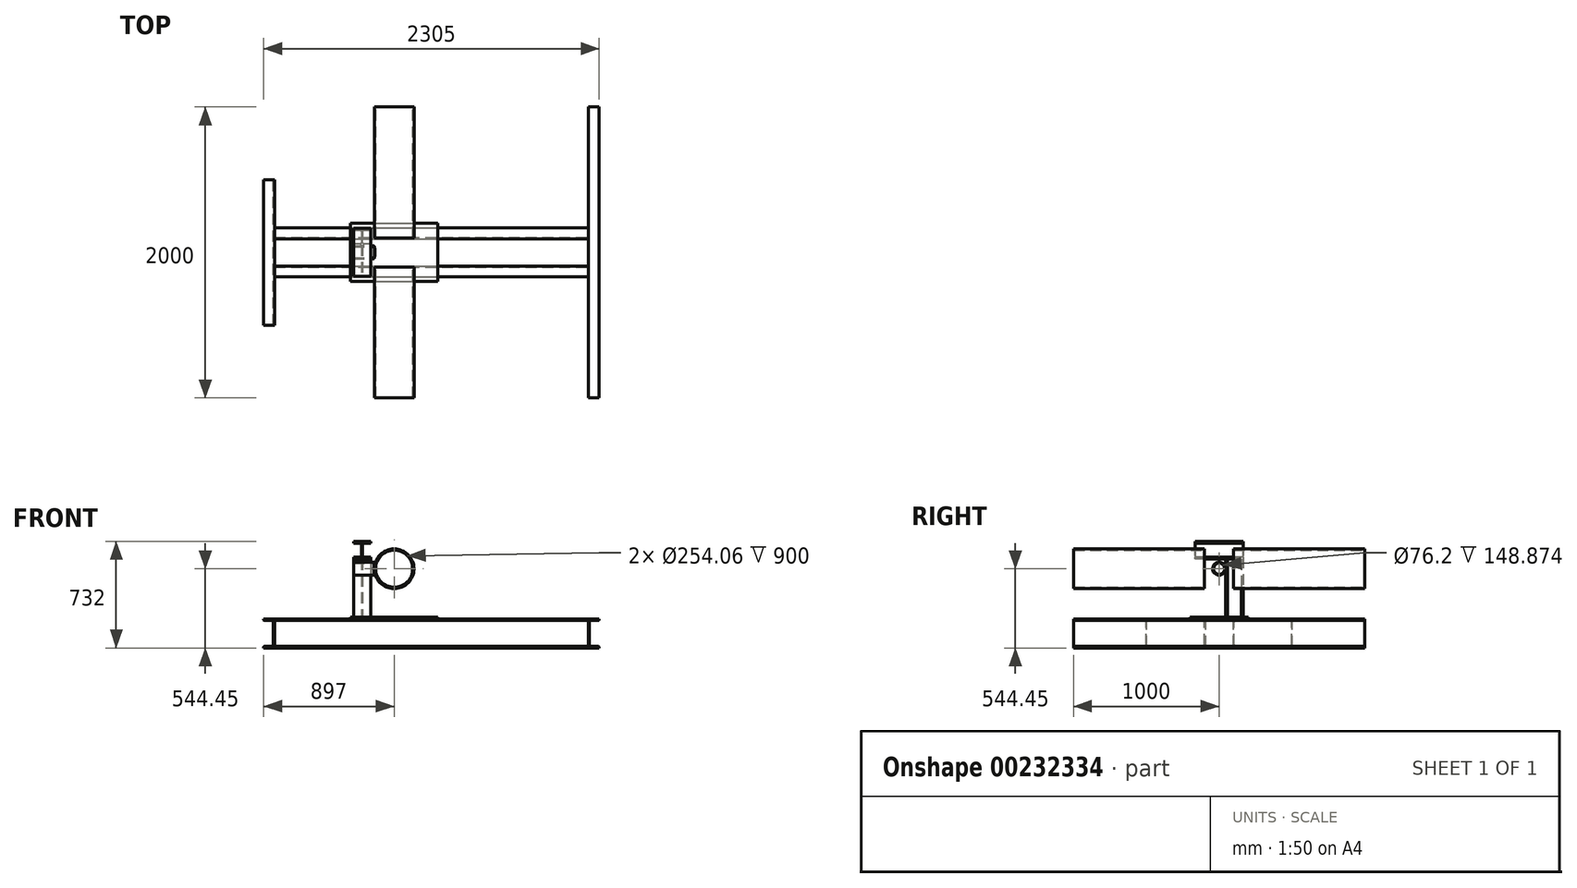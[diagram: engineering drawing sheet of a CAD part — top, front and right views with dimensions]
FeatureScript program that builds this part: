
annotation { "Feature Type Name" : "Feature", "Feature Type Description" : "" }
export const myFeature = defineFeature(function(context is Context, id is Id, definition is map)
    precondition{}
    {
        {
            var Q0;
            Q0=qCreatedBy(makeId("Front.planeOp"),FACE);
            var sketch = newSketch(context, id + "F0", { "sketchPlane" : qUnion([Q0])});
            skCircle(sketch, "E0", {"center": v(0, 0) * mm, "radius": 136.55 * mm});
            skCircle(sketch, "E1", {"center": v(0, 0) * mm, "radius": 127.03 * mm});
            skSolve(sketch);
        }
        {
            var Q0;
            Q0=makeQuery(id+"F0.imprint","IMPRINT",FACE,{"disambiguationData":[TD([[makeQuery(id+"F0.imprint","IMPRINT",EDGE,{"derivedFrom":sQuery(id+"F0.wireOp",EDGE,"E0")}),1.0]])]});
            extrude(context, id + "F1", {"entities" : qUnion([Q0]), "endBound" : BoundingType.SYMMETRIC, "depth" : 2000 * mm});
        }
        {
            var Q0;
            Q0=qCreatedBy(makeId("Right.planeOp"),FACE);
            var sketch = newSketch(context, id + "F2", { "sketchPlane" : qUnion([Q0])});
            skCircle(sketch, "E2", {"center": v(0, 0) * mm, "radius": 44.45 * mm});
            skCircle(sketch, "E3", {"center": v(0, 0) * mm, "radius": 38.1 * mm});
            skSolve(sketch);
        }
        {
            var Q0;
            Q0=qCreatedBy(makeId("Right.planeOp"),FACE);
            var sketch = newSketch(context, id + "F3", { "sketchPlane" : qUnion([Q0])});
            skLineSegment(sketch, "E4", {"start": v(-169, -344.45) * mm, "end": v(-94, -344.45) * mm});
            skLineSegment(sketch, "E5", {"start": v(-94, -344.45) * mm, "end": v(-94, -544.45) * mm});
            skLineSegment(sketch, "E6", {"start": v(-94, -544.45) * mm, "end": v(-169, -544.45) * mm});
            skLineSegment(sketch, "E7", {"start": v(-169, -544.45) * mm, "end": v(-169, -538.95) * mm});
            skLineSegment(sketch, "E8", {"start": v(-163, -532.95) * mm, "end": v(-114, -532.95) * mm});
            skLineSegment(sketch, "E9", {"start": v(-102.5, -521.45) * mm, "end": v(-102.5, -367.45) * mm});
            skLineSegment(sketch, "E10", {"start": v(-114, -355.95) * mm, "end": v(-163, -355.95) * mm});
            skLineSegment(sketch, "E11", {"start": v(-169, -349.95) * mm, "end": v(-169, -344.45) * mm});
            skPoint(sketch, "E12.visualSharp", {"position": v(-102.5, -355.95) * mm});
            skArc(sketch, "E12.filletArc", {"start": v(-102.5, -367.45) * mm, "mid": v(-105.87, -359.32) * mm, "end": v(-114, -355.95) * mm});
            skPoint(sketch, "E13.visualSharp", {"position": v(-102.5, -532.95) * mm});
            skArc(sketch, "E13.filletArc", {"start": v(-114, -532.95) * mm, "mid": v(-105.87, -529.58) * mm, "end": v(-102.5, -521.45) * mm});
            skPoint(sketch, "E14.visualSharp", {"position": v(-169, -355.95) * mm});
            skArc(sketch, "E14.filletArc", {"start": v(-169, -349.95) * mm, "mid": v(-167.24, -354.2) * mm, "end": v(-163, -355.95) * mm});
            skPoint(sketch, "E15.visualSharp", {"position": v(-169, -532.95) * mm});
            skArc(sketch, "E15.filletArc", {"start": v(-163, -532.95) * mm, "mid": v(-167.24, -534.7) * mm, "end": v(-169, -538.95) * mm});
            skLineSegment(sketch, "E16", {"start": v(0, 0) * mm, "end": v(0, -750.46) * mm, "construction": true});
            skSolve(sketch);
        }
        {
            var Q0;
            Q0=makeQuery(id+"F3.imprint","IMPRINT",FACE,{"disambiguationData":[TD([[makeQuery(id+"F3.imprint","IMPRINT",EDGE,{"derivedFrom":sQuery(id+"F3.wireOp",EDGE,"E4")}),-1.0]])]});
            extrude(context, id + "F4", {"entities" : qUnion([Q0]), "oppositeDirection" : true, "depth" : 822 * mm, "hasSecondDirection" : true, "secondDirectionOppositeDirection" : false, "secondDirectionDepth" : (2155 - 822) * mm});
        }
        {
            var Q0;
            Q0=makeQuery(id+"F4.opExtrude","SWEPT_BODY",BODY,{"disambiguationData":[OSD([sQuery(id+"F3.wireOp",EDGE,"E4"),sQuery(id+"F3.wireOp",EDGE,"E5"),sQuery(id+"F3.wireOp",EDGE,"E6"),sQuery(id+"F3.wireOp",EDGE,"E7"),sQuery(id+"F3.wireOp",EDGE,"E8"),sQuery(id+"F3.wireOp",EDGE,"E9"),sQuery(id+"F3.wireOp",EDGE,"E10"),sQuery(id+"F3.wireOp",EDGE,"E11"),sQuery(id+"F3.wireOp",EDGE,"E12.filletArc"),sQuery(id+"F3.wireOp",EDGE,"E13.filletArc"),sQuery(id+"F3.wireOp",EDGE,"E14.filletArc"),sQuery(id+"F3.wireOp",EDGE,"E15.filletArc")])]});
            var Q1;
            Q1=qCreatedBy(makeId("Front.planeOp"),FACE);
            mirror(context, id + "F5", {"entities" : qUnion([Q0]), "mirrorPlane" : qUnion([Q1])});
        }
        {
            var Q0;
            Q0=qCreatedBy(makeId("Front.planeOp"),FACE);
            var sketch = newSketch(context, id + "F6", { "sketchPlane" : qUnion([Q0])});
            skLineSegment(sketch, "E17", {"start": v(-897, -344.45) * mm, "end": v(-822, -344.45) * mm});
            skLineSegment(sketch, "E18", {"start": v(-822, -344.45) * mm, "end": v(-822, -544.45) * mm});
            skLineSegment(sketch, "E19", {"start": v(-822, -544.45) * mm, "end": v(-897, -544.45) * mm});
            skLineSegment(sketch, "E20", {"start": v(-897, -544.45) * mm, "end": v(-897, -538.95) * mm});
            skLineSegment(sketch, "E21", {"start": v(-891, -532.95) * mm, "end": v(-842, -532.95) * mm});
            skLineSegment(sketch, "E22", {"start": v(-830.5, -521.45) * mm, "end": v(-830.5, -367.45) * mm});
            skLineSegment(sketch, "E23", {"start": v(-842, -355.95) * mm, "end": v(-891, -355.95) * mm});
            skLineSegment(sketch, "E24", {"start": v(-897, -349.95) * mm, "end": v(-897, -344.45) * mm});
            skPoint(sketch, "E25.visualSharp", {"position": v(-830.5, -355.95) * mm});
            skArc(sketch, "E25.filletArc", {"start": v(-830.5, -367.45) * mm, "mid": v(-833.87, -359.32) * mm, "end": v(-842, -355.95) * mm});
            skPoint(sketch, "E26.visualSharp", {"position": v(-830.5, -532.95) * mm});
            skArc(sketch, "E26.filletArc", {"start": v(-842, -532.95) * mm, "mid": v(-833.87, -529.58) * mm, "end": v(-830.5, -521.45) * mm});
            skPoint(sketch, "E27.visualSharp", {"position": v(-897, -355.95) * mm});
            skArc(sketch, "E27.filletArc", {"start": v(-897, -349.95) * mm, "mid": v(-895.24, -354.2) * mm, "end": v(-891, -355.95) * mm});
            skPoint(sketch, "E28.visualSharp", {"position": v(-897, -532.95) * mm});
            skArc(sketch, "E28.filletArc", {"start": v(-891, -532.95) * mm, "mid": v(-895.24, -534.7) * mm, "end": v(-897, -538.95) * mm});
            skLineSegment(sketch, "E29", {"start": v(1258, -344.45) * mm, "end": v(1333, -344.45) * mm});
            skLineSegment(sketch, "E30", {"start": v(1333, -344.45) * mm, "end": v(1333, -544.45) * mm});
            skLineSegment(sketch, "E31", {"start": v(1333, -544.45) * mm, "end": v(1258, -544.45) * mm});
            skLineSegment(sketch, "E32", {"start": v(1258, -544.45) * mm, "end": v(1258, -538.95) * mm});
            skLineSegment(sketch, "E33", {"start": v(1264, -532.95) * mm, "end": v(1313, -532.95) * mm});
            skLineSegment(sketch, "E34", {"start": v(1324.5, -521.45) * mm, "end": v(1324.5, -367.45) * mm});
            skLineSegment(sketch, "E35", {"start": v(1313, -355.95) * mm, "end": v(1264, -355.95) * mm});
            skLineSegment(sketch, "E36", {"start": v(1258, -349.95) * mm, "end": v(1258, -344.45) * mm});
            skPoint(sketch, "E37.visualSharp", {"position": v(1324.5, -355.95) * mm});
            skArc(sketch, "E37.filletArc", {"start": v(1324.5, -367.45) * mm, "mid": v(1321.13, -359.32) * mm, "end": v(1313, -355.95) * mm});
            skPoint(sketch, "E38.visualSharp", {"position": v(1324.5, -532.95) * mm});
            skArc(sketch, "E38.filletArc", {"start": v(1313, -532.95) * mm, "mid": v(1321.13, -529.58) * mm, "end": v(1324.5, -521.45) * mm});
            skPoint(sketch, "E39.visualSharp", {"position": v(1258, -355.95) * mm});
            skArc(sketch, "E39.filletArc", {"start": v(1258, -349.95) * mm, "mid": v(1259.76, -354.2) * mm, "end": v(1264, -355.95) * mm});
            skPoint(sketch, "E40.visualSharp", {"position": v(1258, -532.95) * mm});
            skArc(sketch, "E40.filletArc", {"start": v(1264, -532.95) * mm, "mid": v(1259.76, -534.7) * mm, "end": v(1258, -538.95) * mm});
            skLineSegment(sketch, "E41.MirrorCS", {"start": v(1408, -544.45) * mm, "end": v(1408, -538.95) * mm});
            skLineSegment(sketch, "E42.MirrorCS", {"start": v(1408, -349.95) * mm, "end": v(1408, -344.45) * mm});
            skArc(sketch, "E43.MirrorCS", {"start": v(1402, -532.95) * mm, "mid": v(1406.24, -534.7) * mm, "end": v(1408, -538.95) * mm});
            skArc(sketch, "E44.MirrorCS", {"start": v(1408, -349.95) * mm, "mid": v(1406.24, -354.2) * mm, "end": v(1402, -355.95) * mm});
            skArc(sketch, "E45.MirrorCS", {"start": v(1353, -532.95) * mm, "mid": v(1344.87, -529.58) * mm, "end": v(1341.5, -521.45) * mm});
            skArc(sketch, "E46.MirrorCS", {"start": v(1341.5, -367.45) * mm, "mid": v(1344.87, -359.32) * mm, "end": v(1353, -355.95) * mm});
            skLineSegment(sketch, "E47.MirrorCS", {"start": v(1333, -544.45) * mm, "end": v(1408, -544.45) * mm});
            skLineSegment(sketch, "E48.MirrorCS", {"start": v(1341.5, -521.45) * mm, "end": v(1341.5, -367.45) * mm});
            skPoint(sketch, "E49.MirrorP", {"position": v(1408, -355.95) * mm});
            skPoint(sketch, "E50.MirrorP", {"position": v(1341.5, -532.95) * mm});
            skPoint(sketch, "E51.MirrorP", {"position": v(1408, -532.95) * mm});
            skLineSegment(sketch, "E52.MirrorCS", {"start": v(1353, -355.95) * mm, "end": v(1402, -355.95) * mm});
            skLineSegment(sketch, "E53.MirrorCS", {"start": v(1408, -344.45) * mm, "end": v(1333, -344.45) * mm});
            skLineSegment(sketch, "E54.MirrorCS", {"start": v(1402, -532.95) * mm, "end": v(1353, -532.95) * mm});
            skSolve(sketch);
        }
        {
            var Q0;
            Q0=makeQuery(id+"F6.imprint","IMPRINT",FACE,{"disambiguationData":[TD([[makeQuery(id+"F6.imprint","IMPRINT",EDGE,{"derivedFrom":sQuery(id+"F6.wireOp",EDGE,"E17")}),-1.0]])]});
            extrude(context, id + "F7", {"entities" : qUnion([Q0]), "endBound" : BoundingType.SYMMETRIC, "depth" : 1000 * mm});
        }
        {
            var Q0;
            Q0=makeQuery(id+"F6.imprint","IMPRINT",FACE,{"disambiguationData":[TD([[makeQuery(id+"F6.imprint","IMPRINT",EDGE,{"derivedFrom":sQuery(id+"F6.wireOp",EDGE,"E30")}),1.0]])]});
            extrude(context, id + "F8", {"entities" : qUnion([Q0]), "endBound" : BoundingType.SYMMETRIC, "depth" : 2000 * mm});
        }
        {
            var Q0;
            Q0=makeQuery(id+"F5.opPattern","COPY",FACE,{"derivedFrom":makeQuery(id+"F4.opExtrude","SWEPT_FACE",FACE,{"disambiguationData":[OSD([sQuery(id+"F3.wireOp",EDGE,"E4")])]}),"instanceName":"1"});
            var sketch = newSketch(context, id + "F9", { "sketchPlane" : qUnion([Q0])});
            skLineSegment(sketch, "E55.bottom", {"start": v(-300, 200) * mm, "end": v(300, 200) * mm});
            skLineSegment(sketch, "E55.top", {"start": v(-300, -200) * mm, "end": v(300, -200) * mm});
            skLineSegment(sketch, "E55.left", {"start": v(-300, 200) * mm, "end": v(-300, -200) * mm});
            skLineSegment(sketch, "E55.right", {"start": v(300, 200) * mm, "end": v(300, -200) * mm});
            skLineSegment(sketch, "E56", {"start": v(-300, 200) * mm, "end": v(300, -200) * mm, "construction": true});
            skSolve(sketch);
        }
        {
            var Q0;
            {var subQ0=sQuery(id+"F9.wireOp",EDGE,"E55.top");Q0=makeQuery(id+"F9.imprint","IMPRINT",FACE,{"disambiguationData":[TD([[makeQuery(id+"F9.imprint","IMPRINT",EDGE,{"derivedFrom":subQ0}),1.0]])]});}
            var Q1;
            {var subQ0=sQuery(id+"F9.wireOp",EDGE,"E55.bottom");Q1=makeQuery(id+"F9.imprint","IMPRINT",FACE,{"disambiguationData":[TD([[makeQuery(id+"F9.imprint","IMPRINT",EDGE,{"derivedFrom":subQ0}),-1.0]])]});}
            var Q2;
            {var subQ0=sQuery(id+"F9.wireOp",EDGE,"E55.left");var subQ1=sQuery(id+"F3.wireOp",EDGE,"E4");var subQ2=makeQuery(id+"F5.opPattern","COPY",EDGE,{"derivedFrom":makeQuery(id+"F4.opExtrude","SWEPT_EDGE",EDGE,{"disambiguationData":[OSD([subQ1,sQuery(id+"F3.wireOp",EDGE,"E11")])]}),"instanceName":"1"});var subQ3=makeQuery(id+"F9.imprint","INTERSECT",VERTEX,{"derivedFrom":[subQ2,subQ0]});Q2=makeQuery(id+"F9.imprint","IMPRINT",FACE,{"disambiguationData":[TD([[makeQuery(id+"F9.imprint","IMPRINT",EDGE,{"disambiguationData":[TD([[subQ3,-1.0]])],"derivedFrom":subQ0}),1.0]])]});}
            extrude(context, id + "F10", {"entities" : qUnion([Q0, Q1, Q2]), "depth" : 12 * mm});
        }
        {
            var Q0;
            Q0=makeQuery(id+"F10.opExtrude","CAP_FACE",FACE,{"disambiguationData":[OSD([sQuery(id+"F9.wireOp",EDGE,"E55.bottom"),sQuery(id+"F9.wireOp",EDGE,"E55.top"),sQuery(id+"F9.wireOp",EDGE,"E55.left"),sQuery(id+"F9.wireOp",EDGE,"E55.right")])],"isStart":false});
            var sketch = newSketch(context, id + "F11", { "sketchPlane" : qUnion([Q0])});
            skLineSegment(sketch, "E57", {"start": v(-280, 45) * mm, "end": v(-160, 45) * mm});
            skLineSegment(sketch, "E58", {"start": v(-160, 45) * mm, "end": v(-160, 56) * mm});
            skLineSegment(sketch, "E59", {"start": v(-160, 56) * mm, "end": v(-204.75, 56) * mm});
            skLineSegment(sketch, "E60", {"start": v(-216.75, 68) * mm, "end": v(-216.75, 142) * mm});
            skLineSegment(sketch, "E61", {"start": v(-204.75, 154) * mm, "end": v(-160, 154) * mm});
            skLineSegment(sketch, "E62", {"start": v(-160, 154) * mm, "end": v(-160, 165) * mm});
            skLineSegment(sketch, "E63", {"start": v(-160, 165) * mm, "end": v(-280, 165) * mm});
            skLineSegment(sketch, "E64", {"start": v(-280, 165) * mm, "end": v(-280, 154) * mm});
            skLineSegment(sketch, "E65", {"start": v(-280, 154) * mm, "end": v(-235.25, 154) * mm});
            skLineSegment(sketch, "E66", {"start": v(-223.25, 142) * mm, "end": v(-223.25, 68) * mm});
            skLineSegment(sketch, "E67", {"start": v(-235.25, 56) * mm, "end": v(-280, 56) * mm});
            skLineSegment(sketch, "E68", {"start": v(-280, 56) * mm, "end": v(-280, 45) * mm});
            skLineSegment(sketch, "E69", {"start": v(-220, 165) * mm, "end": v(-220, 45) * mm, "construction": true});
            skPoint(sketch, "E70.visualSharp", {"position": v(-223.25, 154) * mm});
            skArc(sketch, "E70.filletArc", {"start": v(-223.25, 142) * mm, "mid": v(-226.76, 150.49) * mm, "end": v(-235.25, 154) * mm});
            skPoint(sketch, "E71.visualSharp", {"position": v(-216.75, 154) * mm});
            skArc(sketch, "E71.filletArc", {"start": v(-204.75, 154) * mm, "mid": v(-213.24, 150.49) * mm, "end": v(-216.75, 142) * mm});
            skPoint(sketch, "E72.visualSharp", {"position": v(-223.25, 56) * mm});
            skArc(sketch, "E72.filletArc", {"start": v(-235.25, 56) * mm, "mid": v(-226.76, 59.51) * mm, "end": v(-223.25, 68) * mm});
            skPoint(sketch, "E73.visualSharp", {"position": v(-216.75, 56) * mm});
            skArc(sketch, "E73.filletArc", {"start": v(-216.75, 68) * mm, "mid": v(-213.24, 59.51) * mm, "end": v(-204.75, 56) * mm});
            skLineSegment(sketch, "E74", {"start": v(0, 0) * mm, "end": v(-497.1, 0) * mm, "construction": true});
            skPoint(sketch, "E74.endSnap0", {"position": v(-300, 0) * mm});
            skLineSegment(sketch, "E75", {"start": v(0, 0) * mm, "end": v(0, 277.06) * mm, "construction": true});
            skSolve(sketch);
        }
        {
            var Q0;
            Q0=makeQuery(id+"F11.imprint","IMPRINT",FACE,{"disambiguationData":[TD([[makeQuery(id+"F11.imprint","IMPRINT",EDGE,{"derivedFrom":sQuery(id+"F11.wireOp",EDGE,"E57")}),1.0]])]});
            extrude(context, id + "F12", {"entities" : qUnion([Q0]), "depth" : 400 * mm});
        }
        {
            var Q0;
            Q0=makeQuery(id+"F2.imprint","IMPRINT",FACE,{"disambiguationData":[TD([[makeQuery(id+"F2.imprint","IMPRINT",EDGE,{"derivedFrom":sQuery(id+"F2.wireOp",EDGE,"E2")}),1.0]])]});
            var Q1;
            Q1=makeQuery(id+"F12.opExtrude","SWEPT_FACE",FACE,{"disambiguationData":[OSD([sQuery(id+"F11.wireOp",EDGE,"E68")])]});
            extrude(context, id + "F13", {"entities" : qUnion([Q0]), "endBound" : BoundingType.UP_TO_SURFACE, "oppositeDirection" : true, "endBoundEntityFace" : qUnion([Q1]), "depth" : 320 * mm});
        }
        {
            var Q0;
            Q0=makeQuery(id+"F0.imprint","IMPRINT",FACE,{"disambiguationData":[TD([[makeQuery(id+"F0.imprint","IMPRINT",EDGE,{"derivedFrom":sQuery(id+"F0.wireOp",EDGE,"E1")}),1.0]])]});
            var Q1;
            Q1=makeQuery(id+"F0.imprint","IMPRINT",FACE,{"disambiguationData":[TD([[makeQuery(id+"F0.imprint","IMPRINT",EDGE,{"derivedFrom":sQuery(id+"F0.wireOp",EDGE,"E0")}),1.0]])]});
            extrude(context, id + "F14", {"entities" : qUnion([Q0, Q1]), "operationType" : NewBodyOperationType.REMOVE, "endBound" : BoundingType.SYMMETRIC, "oppositeDirection" : true, "depth" : 200 * mm});
        }
        {
            var Q0;
            Q0=makeQuery(id+"F14.boolean.opBoolean","INTERSECT",EDGE,{"derivedFrom":[makeQuery(id+"F13.opExtrude","SWEPT_FACE",FACE,{"disambiguationData":[OSD([sQuery(id+"F2.wireOp",EDGE,"E2")])]}),makeQuery(id+"F14.opExtrude","SWEPT_FACE",FACE,{"disambiguationData":[OSD([sQuery(id+"F0.wireOp",EDGE,"E0")])]})]});
            chamfer(context, id + "F15", {"entities" : qUnion([Q0]), "width" : 4 * mm, "tangentPropagation" : true});
        }
        {
            var Q0;
            Q0=qCreatedBy(makeId("Front.planeOp"),FACE);
            var sketch = newSketch(context, id + "F16", { "sketchPlane" : qUnion([Q0])});
            skLineSegment(sketch, "E76", {"start": v(-280, 67.55) * mm, "end": v(-160, 67.55) * mm});
            skLineSegment(sketch, "E77", {"start": v(-160, 67.55) * mm, "end": v(-160, 78.55) * mm});
            skLineSegment(sketch, "E78", {"start": v(-160, 78.55) * mm, "end": v(-204.75, 78.55) * mm});
            skLineSegment(sketch, "E79", {"start": v(-216.75, 90.55) * mm, "end": v(-216.75, 164.55) * mm});
            skLineSegment(sketch, "E80", {"start": v(-204.75, 176.55) * mm, "end": v(-160, 176.55) * mm});
            skLineSegment(sketch, "E81", {"start": v(-160, 176.55) * mm, "end": v(-160, 187.55) * mm});
            skLineSegment(sketch, "E82", {"start": v(-160, 187.55) * mm, "end": v(-280, 187.55) * mm});
            skLineSegment(sketch, "E83", {"start": v(-280, 187.55) * mm, "end": v(-280, 176.55) * mm});
            skLineSegment(sketch, "E84", {"start": v(-280, 176.55) * mm, "end": v(-235.25, 176.55) * mm});
            skLineSegment(sketch, "E85", {"start": v(-223.25, 164.55) * mm, "end": v(-223.25, 90.55) * mm});
            skLineSegment(sketch, "E86", {"start": v(-235.25, 78.55) * mm, "end": v(-280, 78.55) * mm});
            skLineSegment(sketch, "E87", {"start": v(-280, 78.55) * mm, "end": v(-280, 67.55) * mm});
            skLineSegment(sketch, "E88", {"start": v(-220, 187.55) * mm, "end": v(-220, 67.55) * mm, "construction": true});
            skPoint(sketch, "E89.visualSharp", {"position": v(-223.25, 176.55) * mm});
            skArc(sketch, "E89.filletArc", {"start": v(-223.25, 164.55) * mm, "mid": v(-226.76, 173.04) * mm, "end": v(-235.25, 176.55) * mm});
            skPoint(sketch, "E90.visualSharp", {"position": v(-216.75, 176.55) * mm});
            skArc(sketch, "E90.filletArc", {"start": v(-204.75, 176.55) * mm, "mid": v(-213.24, 173.04) * mm, "end": v(-216.75, 164.55) * mm});
            skPoint(sketch, "E91.visualSharp", {"position": v(-223.25, 78.55) * mm});
            skArc(sketch, "E91.filletArc", {"start": v(-235.25, 78.55) * mm, "mid": v(-226.76, 82.06) * mm, "end": v(-223.25, 90.55) * mm});
            skPoint(sketch, "E92.visualSharp", {"position": v(-216.75, 78.55) * mm});
            skArc(sketch, "E92.filletArc", {"start": v(-216.75, 90.55) * mm, "mid": v(-213.24, 82.06) * mm, "end": v(-204.75, 78.55) * mm});
            skSolve(sketch);
        }
        {
            var Q0;
            Q0=makeQuery(id+"F16.imprint","IMPRINT",FACE,{"disambiguationData":[TD([[makeQuery(id+"F16.imprint","IMPRINT",EDGE,{"derivedFrom":sQuery(id+"F16.wireOp",EDGE,"E76")}),1.0]])]});
            var Q1;
            Q1=makeQuery(id+"F12.opExtrude","SWEPT_FACE",FACE,{"disambiguationData":[OSD([sQuery(id+"F11.wireOp",EDGE,"E63")])]});
            extrude(context, id + "F17", {"entities" : qUnion([Q0]), "endBound" : BoundingType.UP_TO_SURFACE, "oppositeDirection" : true, "endBoundEntityFace" : qUnion([Q1]), "depth" : 25 * mm});
        }
        {
            var Q0;
            Q0=makeQuery(id+"F17.opExtrude","SWEPT_BODY",BODY,{"disambiguationData":[OSD([sQuery(id+"F16.wireOp",EDGE,"E76"),sQuery(id+"F16.wireOp",EDGE,"E77"),sQuery(id+"F16.wireOp",EDGE,"E78"),sQuery(id+"F16.wireOp",EDGE,"E79"),sQuery(id+"F16.wireOp",EDGE,"E80"),sQuery(id+"F16.wireOp",EDGE,"E81"),sQuery(id+"F16.wireOp",EDGE,"E82"),sQuery(id+"F16.wireOp",EDGE,"E83"),sQuery(id+"F16.wireOp",EDGE,"E84"),sQuery(id+"F16.wireOp",EDGE,"E85"),sQuery(id+"F16.wireOp",EDGE,"E86"),sQuery(id+"F16.wireOp",EDGE,"E87"),sQuery(id+"F16.wireOp",EDGE,"E89.filletArc"),sQuery(id+"F16.wireOp",EDGE,"E90.filletArc"),sQuery(id+"F16.wireOp",EDGE,"E91.filletArc"),sQuery(id+"F16.wireOp",EDGE,"E92.filletArc")])]});
            var Q1;
            Q1=qCreatedBy(makeId("Front.planeOp"),FACE);
            mirror(context, id + "F18", {"operationType" : NewBodyOperationType.ADD, "entities" : qUnion([Q0]), "mirrorPlane" : qUnion([Q1])});
        }
    });
